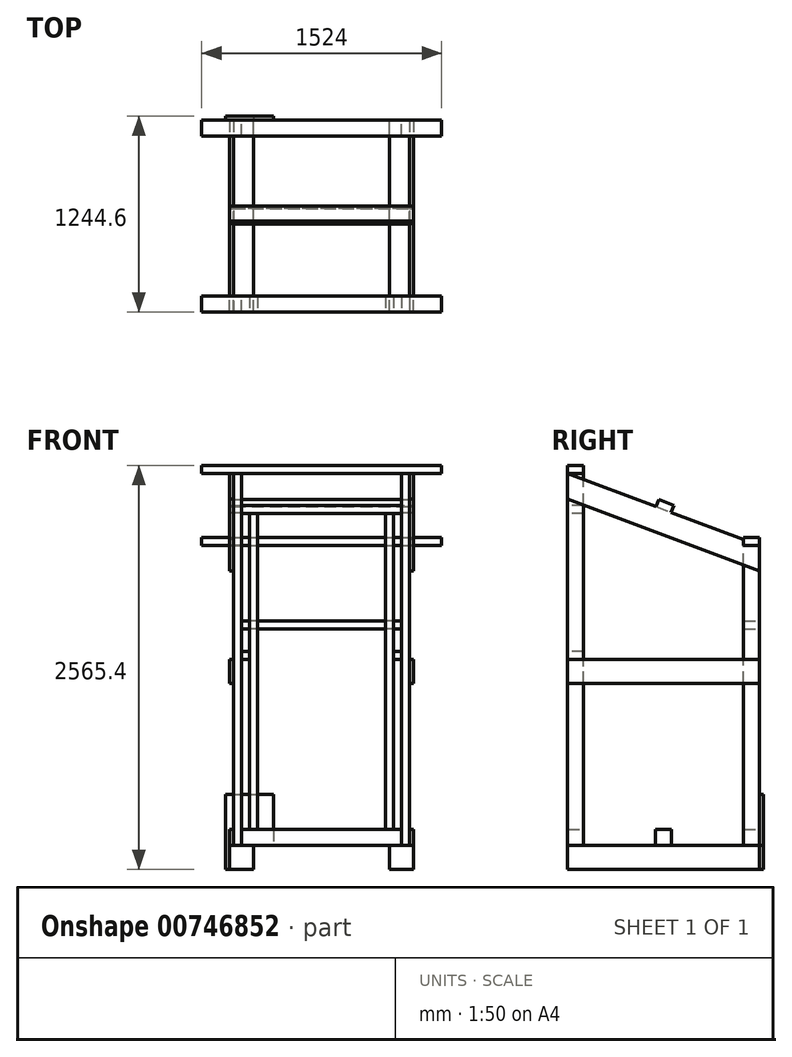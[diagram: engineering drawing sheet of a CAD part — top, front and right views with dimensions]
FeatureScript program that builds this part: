
annotation { "Feature Type Name" : "Feature", "Feature Type Description" : "" }
export const myFeature = defineFeature(function(context is Context, id is Id, definition is map)
    precondition{}
    {
        {
            var Q0;
            Q0=qCreatedBy(makeId("Front.planeOp"),FACE);
            var sketch = newSketch(context, id + "F0", { "sketchPlane" : qUnion([Q0])});
            skLineSegment(sketch, "E0.bottom", {"start": v(0, 0) * mm, "end": v(152.4, 0) * mm});
            skLineSegment(sketch, "E0.top", {"start": v(0, 152.4) * mm, "end": v(152.4, 152.4) * mm});
            skLineSegment(sketch, "E0.left", {"start": v(0, 0) * mm, "end": v(0, 152.4) * mm});
            skLineSegment(sketch, "E0.right", {"start": v(152.4, 0) * mm, "end": v(152.4, 152.4) * mm});
            skLineSegment(sketch, "E1.bottom", {"start": v(1016, 0) * mm, "end": v(1168.4, 0) * mm});
            skLineSegment(sketch, "E1.top", {"start": v(1016, 152.4) * mm, "end": v(1168.4, 152.4) * mm});
            skLineSegment(sketch, "E1.left", {"start": v(1016, 0) * mm, "end": v(1016, 152.4) * mm});
            skLineSegment(sketch, "E1.right", {"start": v(1168.4, 0) * mm, "end": v(1168.4, 152.4) * mm});
            skLineSegment(sketch, "E2.bottom", {"start": v(0, 152.4) * mm, "end": v(1168.4, 152.4) * mm});
            skLineSegment(sketch, "E2.top", {"start": v(0, 254) * mm, "end": v(1168.4, 254) * mm});
            skLineSegment(sketch, "E2.left", {"start": v(0, 152.4) * mm, "end": v(0, 254) * mm});
            skLineSegment(sketch, "E2.right", {"start": v(1168.4, 152.4) * mm, "end": v(1168.4, 254) * mm});
            skLineSegment(sketch, "E3.bottom", {"start": v(0, 152.4) * mm, "end": v(76.2, 152.4) * mm});
            skLineSegment(sketch, "E3.top", {"start": v(0, 254) * mm, "end": v(76.2, 254) * mm});
            skLineSegment(sketch, "E3.right", {"start": v(76.2, 152.4) * mm, "end": v(76.2, 254) * mm});
            skLineSegment(sketch, "E4.bottom", {"start": v(1168.4, 254) * mm, "end": v(1092.2, 254) * mm});
            skLineSegment(sketch, "E4.top", {"start": v(1168.4, 152.4) * mm, "end": v(1092.2, 152.4) * mm});
            skLineSegment(sketch, "E4.left", {"start": v(1168.4, 254) * mm, "end": v(1168.4, 152.4) * mm});
            skLineSegment(sketch, "E4.right", {"start": v(1092.2, 254) * mm, "end": v(1092.2, 152.4) * mm});
            skSolve(sketch);
        }
        {
            var Q0;
            Q0=makeQuery(id+"F0.imprint","IMPRINT",FACE,{"disambiguationData":[TD([[makeQuery(id+"F0.imprint","IMPRINT",EDGE,{"derivedFrom":sQuery(id+"F0.wireOp",EDGE,"E0.bottom")}),1.0]])]});
            var Q1;
            Q1=makeQuery(id+"F0.imprint","IMPRINT",FACE,{"disambiguationData":[TD([[makeQuery(id+"F0.imprint","IMPRINT",EDGE,{"derivedFrom":sQuery(id+"F0.wireOp",EDGE,"E1.bottom")}),1.0]])]});
            extrude(context, id + "F1", {"entities" : qUnion([Q0, Q1]), "depth" : 1219.2 * mm, "offsetDistance" : 25 * mm});
        }
        {
            var Q0;
            {var subQ3=sQuery(id+"F0.wireOp",EDGE,"E2.bottom");Q0=makeQuery(id+"F0.imprint","IMPRINT",FACE,{"disambiguationData":[TD([[makeQuery(id+"F0.imprint","IMPRINT",EDGE,{"derivedFrom":subQ3}),1.0]])]});}
            extrude(context, id + "F2", {"entities" : qUnion([Q0]), "depth" : 101.6 * mm, "offsetDistance" : 25 * mm});
        }
        {
            var Q0;
            Q0=makeQuery(id+"F2.opExtrude","SWEPT_BODY",BODY,{"disambiguationData":[OSD([sQuery(id+"F0.wireOp",EDGE,"E0.top"),sQuery(id+"F0.wireOp",EDGE,"E1.top"),sQuery(id+"F0.wireOp",EDGE,"E2.bottom"),sQuery(id+"F0.wireOp",EDGE,"E2.top"),sQuery(id+"F0.wireOp",EDGE,"E3.right"),sQuery(id+"F0.wireOp",EDGE,"E4.right")])]});
            var Q1;
            Q1=makeQuery(id+"F2.opExtrude","CAP_FACE",FACE,{"disambiguationData":[OSD([sQuery(id+"F0.wireOp",EDGE,"E0.top"),sQuery(id+"F0.wireOp",EDGE,"E1.top"),sQuery(id+"F0.wireOp",EDGE,"E2.bottom"),sQuery(id+"F0.wireOp",EDGE,"E2.top"),sQuery(id+"F0.wireOp",EDGE,"E3.right"),sQuery(id+"F0.wireOp",EDGE,"E4.right")])],"isStart":false});
            transform(context, id + "F3", {"entities" : qUnion([Q0]), "transformType" : TransformType.TRANSLATION_DISTANCE, "transformDirection" : qUnion([Q1]), "distance" : 1117.6 * mm, "makeCopy" : true});
        }
        {
            var Q0;
            Q0=makeQuery(id+"F1.opExtrude","SWEPT_FACE",FACE,{"disambiguationData":[OSD([sQuery(id+"F0.wireOp",EDGE,"E0.top")])]});
            var sketch = newSketch(context, id + "F4", { "sketchPlane" : qUnion([Q0])});
            skLineSegment(sketch, "E5.bottom", {"start": v(0, -609.6) * mm, "end": v(1168.4, -609.6) * mm});
            skLineSegment(sketch, "E5.top", {"start": v(0, -660.4) * mm, "end": v(1168.4, -660.4) * mm});
            skLineSegment(sketch, "E5.left", {"start": v(0, -609.6) * mm, "end": v(0, -660.4) * mm});
            skLineSegment(sketch, "E5.right", {"start": v(1168.4, -609.6) * mm, "end": v(1168.4, -660.4) * mm});
            skLineSegment(sketch, "E6.MirrorCS", {"start": v(0, -609.6) * mm, "end": v(0, -558.8) * mm});
            skLineSegment(sketch, "E7.MirrorCS", {"start": v(0, -558.8) * mm, "end": v(1168.4, -558.8) * mm});
            skLineSegment(sketch, "E8.MirrorCS", {"start": v(1168.4, -609.6) * mm, "end": v(1168.4, -558.8) * mm});
            skSolve(sketch);
        }
        {
            var Q0;
            {var subQ0=sQuery(id+"F4.wireOp",EDGE,"E6.MirrorCS");Q0=makeQuery(id+"F4.imprint","IMPRINT",FACE,{"disambiguationData":[TD([[makeQuery(id+"F4.imprint","IMPRINT",EDGE,{"derivedFrom":subQ0}),-1.0]])]});}
            var Q1;
            {var subQ0=sQuery(id+"F4.wireOp",EDGE,"E5.left");Q1=makeQuery(id+"F4.imprint","IMPRINT",FACE,{"disambiguationData":[TD([[makeQuery(id+"F4.imprint","IMPRINT",EDGE,{"derivedFrom":subQ0}),-1.0]])]});}
            var Q2;
            {var subQ0=sQuery(id+"F4.wireOp",EDGE,"E5.right");Q2=makeQuery(id+"F4.imprint","IMPRINT",FACE,{"disambiguationData":[TD([[makeQuery(id+"F4.imprint","IMPRINT",EDGE,{"derivedFrom":subQ0}),-1.0]])]});}
            var Q3;
            {var subQ0=sQuery(id+"F4.wireOp",EDGE,"E8.MirrorCS");Q3=makeQuery(id+"F4.imprint","IMPRINT",FACE,{"disambiguationData":[TD([[makeQuery(id+"F4.imprint","IMPRINT",EDGE,{"derivedFrom":subQ0}),1.0]])]});}
            extrude(context, id + "F5", {"entities" : qUnion([Q0, Q1, Q2, Q3]), "depth" : 101.6 * mm, "offsetDistance" : 25 * mm});
        }
        {
            var Q0;
            Q0=makeQuery(id+"F3.opPattern","COPY",FACE,{"derivedFrom":makeQuery(id+"F2.opExtrude","CAP_FACE",FACE,{"disambiguationData":[OSD([sQuery(id+"F0.wireOp",EDGE,"E0.top"),sQuery(id+"F0.wireOp",EDGE,"E1.top"),sQuery(id+"F0.wireOp",EDGE,"E2.bottom"),sQuery(id+"F0.wireOp",EDGE,"E2.top"),sQuery(id+"F0.wireOp",EDGE,"E3.right"),sQuery(id+"F0.wireOp",EDGE,"E4.right")])],"isStart":false}),"instanceName":"1"});
            var sketch = newSketch(context, id + "F6", { "sketchPlane" : qUnion([Q0])});
            skLineSegment(sketch, "E9.bottom", {"start": v(76.2, 152.4) * mm, "end": v(25.4, 152.4) * mm});
            skLineSegment(sketch, "E9.top", {"start": v(76.2, 2514.6) * mm, "end": v(25.4, 2514.6) * mm});
            skLineSegment(sketch, "E9.left", {"start": v(76.2, 152.4) * mm, "end": v(76.2, 2514.6) * mm});
            skLineSegment(sketch, "E9.right", {"start": v(25.4, 152.4) * mm, "end": v(25.4, 2514.6) * mm});
            skLineSegment(sketch, "E10.bottom", {"start": v(1092.2, 152.4) * mm, "end": v(1143, 152.4) * mm});
            skLineSegment(sketch, "E10.top", {"start": v(1092.2, 2514.6) * mm, "end": v(1143, 2514.6) * mm});
            skLineSegment(sketch, "E10.left", {"start": v(1092.2, 152.4) * mm, "end": v(1092.2, 2514.6) * mm});
            skLineSegment(sketch, "E10.right", {"start": v(1143, 152.4) * mm, "end": v(1143, 2514.6) * mm});
            skLineSegment(sketch, "E11.bottom", {"start": v(127, 254) * mm, "end": v(177.8, 254) * mm});
            skLineSegment(sketch, "E11.top", {"start": v(127, 2260.6) * mm, "end": v(177.8, 2260.6) * mm});
            skLineSegment(sketch, "E11.left", {"start": v(127, 254) * mm, "end": v(127, 2260.6) * mm});
            skLineSegment(sketch, "E11.right", {"start": v(177.8, 254) * mm, "end": v(177.8, 2260.6) * mm});
            skLineSegment(sketch, "E12.bottom", {"start": v(1041.4, 254) * mm, "end": v(990.6, 254) * mm});
            skLineSegment(sketch, "E12.top", {"start": v(1041.4, 2260.6) * mm, "end": v(990.6, 2260.6) * mm});
            skLineSegment(sketch, "E12.left", {"start": v(1041.4, 254) * mm, "end": v(1041.4, 2260.6) * mm});
            skLineSegment(sketch, "E12.right", {"start": v(990.6, 254) * mm, "end": v(990.6, 2260.6) * mm});
            skLineSegment(sketch, "E13.bottom", {"start": v(76.2, 2260.6) * mm, "end": v(1092.2, 2260.6) * mm});
            skLineSegment(sketch, "E13.top", {"start": v(76.2, 2311.4) * mm, "end": v(1092.2, 2311.4) * mm});
            skLineSegment(sketch, "E13.left", {"start": v(76.2, 2260.6) * mm, "end": v(76.2, 2311.4) * mm});
            skLineSegment(sketch, "E13.right", {"start": v(1092.2, 2260.6) * mm, "end": v(1092.2, 2311.4) * mm});
            skLineSegment(sketch, "E14", {"start": v(584.2, 2311.4) * mm, "end": v(584.2, 2514.6) * mm, "construction": true});
            skLineSegment(sketch, "E15.bottom", {"start": v(584.2, 2514.6) * mm, "end": v(-177.8, 2514.6) * mm});
            skLineSegment(sketch, "E15.top", {"start": v(584.2, 2565.4) * mm, "end": v(-177.8, 2565.4) * mm});
            skLineSegment(sketch, "E15.left", {"start": v(584.2, 2514.6) * mm, "end": v(584.2, 2565.4) * mm});
            skLineSegment(sketch, "E15.right", {"start": v(-177.8, 2514.6) * mm, "end": v(-177.8, 2565.4) * mm});
            skLineSegment(sketch, "E16.MirrorCS", {"start": v(584.2, 2565.4) * mm, "end": v(1346.2, 2565.4) * mm});
            skLineSegment(sketch, "E17.MirrorCS", {"start": v(584.2, 2514.6) * mm, "end": v(1346.2, 2514.6) * mm});
            skLineSegment(sketch, "E18.MirrorCS", {"start": v(1346.2, 2514.6) * mm, "end": v(1346.2, 2565.4) * mm});
            skLineSegment(sketch, "E19.bottom", {"start": v(25.4, 1333.5) * mm, "end": v(0, 1333.5) * mm});
            skLineSegment(sketch, "E19.top", {"start": v(25.4, 1181.1) * mm, "end": v(0, 1181.1) * mm});
            skLineSegment(sketch, "E19.left", {"start": v(25.4, 1333.5) * mm, "end": v(25.4, 1181.1) * mm});
            skLineSegment(sketch, "E19.right", {"start": v(0, 1333.5) * mm, "end": v(0, 1181.1) * mm});
            skLineSegment(sketch, "E20.bottom", {"start": v(1143, 1333.5) * mm, "end": v(1168.4, 1333.5) * mm});
            skLineSegment(sketch, "E20.top", {"start": v(1143, 1181.1) * mm, "end": v(1168.4, 1181.1) * mm});
            skLineSegment(sketch, "E20.left", {"start": v(1143, 1333.5) * mm, "end": v(1143, 1181.1) * mm});
            skLineSegment(sketch, "E20.right", {"start": v(1168.4, 1333.5) * mm, "end": v(1168.4, 1181.1) * mm});
            skLineSegment(sketch, "E21.bottom", {"start": v(76.2, 1333.5) * mm, "end": v(127, 1333.5) * mm});
            skLineSegment(sketch, "E21.top", {"start": v(76.2, 1384.3) * mm, "end": v(127, 1384.3) * mm});
            skLineSegment(sketch, "E21.left", {"start": v(76.2, 1333.5) * mm, "end": v(76.2, 1384.3) * mm});
            skLineSegment(sketch, "E21.right", {"start": v(127, 1333.5) * mm, "end": v(127, 1384.3) * mm});
            skLineSegment(sketch, "E22.bottom", {"start": v(1092.2, 1333.5) * mm, "end": v(1041.4, 1333.5) * mm});
            skLineSegment(sketch, "E22.top", {"start": v(1092.2, 1384.3) * mm, "end": v(1041.4, 1384.3) * mm});
            skLineSegment(sketch, "E22.left", {"start": v(1092.2, 1333.5) * mm, "end": v(1092.2, 1384.3) * mm});
            skLineSegment(sketch, "E22.right", {"start": v(1041.4, 1333.5) * mm, "end": v(1041.4, 1384.3) * mm});
            skSolve(sketch);
        }
        {
            var Q0;
            {var subQ1=sQuery(id+"F6.wireOp",EDGE,"E9.bottom");Q0=makeQuery(id+"F6.imprint","IMPRINT",FACE,{"disambiguationData":[TD([[makeQuery(id+"F6.imprint","IMPRINT",EDGE,{"derivedFrom":subQ1}),-1.0]])]});}
            var Q1;
            {var subQ3=sQuery(id+"F6.wireOp",EDGE,"E10.bottom");Q1=makeQuery(id+"F6.imprint","IMPRINT",FACE,{"disambiguationData":[TD([[makeQuery(id+"F6.imprint","IMPRINT",EDGE,{"derivedFrom":subQ3}),1.0]])]});}
            extrude(context, id + "F7", {"entities" : qUnion([Q0, Q1]), "depth" : -101.6 * mm, "offsetDistance" : 25 * mm});
        }
        {
            var Q0;
            Q0=makeQuery(id+"F2.opExtrude","CAP_FACE",FACE,{"disambiguationData":[OSD([sQuery(id+"F0.wireOp",EDGE,"E0.top"),sQuery(id+"F0.wireOp",EDGE,"E1.top"),sQuery(id+"F0.wireOp",EDGE,"E2.bottom"),sQuery(id+"F0.wireOp",EDGE,"E2.top"),sQuery(id+"F0.wireOp",EDGE,"E3.right"),sQuery(id+"F0.wireOp",EDGE,"E4.right")])],"isStart":true});
            var sketch = newSketch(context, id + "F8", { "sketchPlane" : qUnion([Q0])});
            skLineSegment(sketch, "E23.bottom", {"start": v(-1092.2, 152.4) * mm, "end": v(-1143, 152.4) * mm});
            skLineSegment(sketch, "E23.top", {"start": v(-1092.2, 2057.4) * mm, "end": v(-1143, 2057.4) * mm});
            skLineSegment(sketch, "E23.left", {"start": v(-1092.2, 152.4) * mm, "end": v(-1092.2, 2057.4) * mm});
            skLineSegment(sketch, "E23.right", {"start": v(-1143, 152.4) * mm, "end": v(-1143, 2057.4) * mm});
            skLineSegment(sketch, "E24.bottom", {"start": v(-76.2, 152.4) * mm, "end": v(-25.4, 152.4) * mm});
            skLineSegment(sketch, "E24.top", {"start": v(-76.2, 2057.4) * mm, "end": v(-25.4, 2057.4) * mm});
            skLineSegment(sketch, "E24.left", {"start": v(-76.2, 152.4) * mm, "end": v(-76.2, 2057.4) * mm});
            skLineSegment(sketch, "E24.right", {"start": v(-25.4, 152.4) * mm, "end": v(-25.4, 2057.4) * mm});
            skSolve(sketch);
        }
        {
            var Q0;
            {var subQ1=sQuery(id+"F8.wireOp",EDGE,"E23.bottom");Q0=makeQuery(id+"F8.imprint","IMPRINT",FACE,{"disambiguationData":[TD([[makeQuery(id+"F8.imprint","IMPRINT",EDGE,{"derivedFrom":subQ1}),-1.0]])]});}
            var Q1;
            {var subQ1=sQuery(id+"F8.wireOp",EDGE,"E24.bottom");Q1=makeQuery(id+"F8.imprint","IMPRINT",FACE,{"disambiguationData":[TD([[makeQuery(id+"F8.imprint","IMPRINT",EDGE,{"derivedFrom":subQ1}),1.0]])]});}
            extrude(context, id + "F9", {"entities" : qUnion([Q0, Q1]), "depth" : -101.6 * mm, "offsetDistance" : 25 * mm});
        }
        {
            var Q0;
            Q0=makeQuery(id+"F6.imprint","IMPRINT",FACE,{"disambiguationData":[TD([[makeQuery(id+"F6.imprint","IMPRINT",EDGE,{"derivedFrom":sQuery(id+"F6.wireOp",EDGE,"E11.bottom")}),1.0]])]});
            var Q1;
            Q1=makeQuery(id+"F6.imprint","IMPRINT",FACE,{"disambiguationData":[TD([[makeQuery(id+"F6.imprint","IMPRINT",EDGE,{"derivedFrom":sQuery(id+"F6.wireOp",EDGE,"E12.bottom")}),1.0]])]});
            extrude(context, id + "F10", {"entities" : qUnion([Q0, Q1]), "depth" : -101.6 * mm, "offsetDistance" : 25 * mm});
        }
        {
            var Q0;
            Q0=makeQuery(id+"F6.imprint","IMPRINT",FACE,{"disambiguationData":[TD([[makeQuery(id+"F6.imprint","IMPRINT",EDGE,{"derivedFrom":sQuery(id+"F6.wireOp",EDGE,"E13.top")}),-1.0]])]});
            var Q1;
            {var subQ3=sQuery(id+"F6.wireOp",EDGE,"E15.left");Q1=makeQuery(id+"F6.imprint","IMPRINT",FACE,{"disambiguationData":[TD([[makeQuery(id+"F6.imprint","IMPRINT",EDGE,{"derivedFrom":subQ3}),-1.0]])]});}
            var Q2;
            Q2=makeQuery(id+"F6.imprint","IMPRINT",FACE,{"disambiguationData":[TD([[makeQuery(id+"F6.imprint","IMPRINT",EDGE,{"derivedFrom":sQuery(id+"F6.wireOp",EDGE,"E15.top")}),1.0]])]});
            extrude(context, id + "F11", {"entities" : qUnion([Q0, Q1, Q2]), "depth" : -101.6 * mm, "offsetDistance" : 25 * mm});
        }
        {
            var Q0;
            Q0=makeQuery(id+"F7.opExtrude","SWEPT_FACE",FACE,{"disambiguationData":[OSD([sQuery(id+"F6.wireOp",EDGE,"E10.right")])]});
            var sketch = newSketch(context, id + "F12", { "sketchPlane" : qUnion([Q0])});
            skLineSegment(sketch, "E25", {"start": v(-1219.2, 2514.6) * mm, "end": v(0, 2057.41) * mm});
            skLineSegment(sketch, "E26", {"start": v(0, 2057.41) * mm, "end": v(0, 1894.65) * mm});
            skLineSegment(sketch, "E27", {"start": v(0, 1894.65) * mm, "end": v(-1219.2, 2351.84) * mm});
            skLineSegment(sketch, "E28", {"start": v(-1219.2, 2351.84) * mm, "end": v(-1219.2, 2514.6) * mm});
            skLineSegment(sketch, "E29", {"start": v(-1219.2, 2351.84) * mm, "end": v(-1219.2, 152.4) * mm, "construction": true});
            skLineSegment(sketch, "E30", {"start": v(-1219.2, 152.4) * mm, "end": v(0, 152.4) * mm, "construction": true});
            skPoint(sketch, "E30.endSnap0", {"position": v(-1168.4, 152.4) * mm});
            skLineSegment(sketch, "E31", {"start": v(0, 152.4) * mm, "end": v(0, 1894.65) * mm, "construction": true});
            skLineSegment(sketch, "E32", {"start": v(0, 2057.41) * mm, "end": v(-101.6, 2057.41) * mm});
            skLineSegment(sketch, "E33", {"start": v(-101.6, 2057.41) * mm, "end": v(-101.6, 2095.51) * mm});
            skLineSegment(sketch, "E34", {"start": v(-609.6, 2286) * mm, "end": v(-592.83, 2330.73) * mm});
            skLineSegment(sketch, "E35", {"start": v(-592.83, 2330.73) * mm, "end": v(-545.26, 2312.9) * mm});
            skLineSegment(sketch, "E36", {"start": v(-545.26, 2312.9) * mm, "end": v(-562.03, 2268.17) * mm});
            skLineSegment(sketch, "E37.MirrorCS", {"start": v(-592.83, 2330.73) * mm, "end": v(-640.4, 2348.57) * mm});
            skLineSegment(sketch, "E38.MirrorCS", {"start": v(0, 2057.41) * mm, "end": v(-1219.2, 2514.6) * mm});
            skLineSegment(sketch, "E39.MirrorCS", {"start": v(-640.4, 2348.57) * mm, "end": v(-657.17, 2303.84) * mm});
            skSolve(sketch);
        }
        {
            var Q0;
            {var subQ0=sQuery(id+"F12.wireOp",EDGE,"E26");Q0=makeQuery(id+"F12.imprint","IMPRINT",FACE,{"disambiguationData":[TD([[makeQuery(id+"F12.imprint","IMPRINT",EDGE,{"derivedFrom":subQ0}),-1.0]])]});}
            var Q1;
            {var subQ0=sQuery(id+"F12.wireOp",EDGE,"E28");Q1=makeQuery(id+"F12.imprint","IMPRINT",FACE,{"disambiguationData":[TD([[makeQuery(id+"F12.imprint","IMPRINT",EDGE,{"derivedFrom":subQ0}),-1.0]])]});}
            extrude(context, id + "F13", {"entities" : qUnion([Q0, Q1]), "depth" : 25.4 * mm, "offsetDistance" : 25 * mm});
        }
        {
            var Q0;
            {var subQ0=sQuery(id+"F12.wireOp",EDGE,"E34");Q0=makeQuery(id+"F12.imprint","IMPRINT",FACE,{"disambiguationData":[TD([[makeQuery(id+"F12.imprint","IMPRINT",EDGE,{"derivedFrom":subQ0}),1.0]])]});}
            var Q1;
            {var subQ0=sQuery(id+"F12.wireOp",EDGE,"E34");Q1=makeQuery(id+"F12.imprint","IMPRINT",FACE,{"disambiguationData":[TD([[makeQuery(id+"F12.imprint","IMPRINT",EDGE,{"derivedFrom":subQ0}),-1.0]])]});}
            extrude(context, id + "F14", {"entities" : qUnion([Q0, Q1]), "depth" : -1117.6 * mm, "offsetDistance" : 25 * mm});
        }
        {
            var Q0;
            Q0=makeQuery(id+"F13.opExtrude","SWEPT_BODY",BODY,{"disambiguationData":[OSD([sQuery(id+"F12.wireOp",EDGE,"E26"),sQuery(id+"F12.wireOp",EDGE,"E27"),sQuery(id+"F12.wireOp",EDGE,"E28"),sQuery(id+"F12.wireOp",EDGE,"E32"),sQuery(id+"F12.wireOp",EDGE,"E33"),sQuery(id+"F12.wireOp",EDGE,"E38.MirrorCS")])]});
            var Q1;
            Q1=makeQuery(id+"F13.opExtrude","CAP_FACE",FACE,{"disambiguationData":[OSD([sQuery(id+"F12.wireOp",EDGE,"E26"),sQuery(id+"F12.wireOp",EDGE,"E27"),sQuery(id+"F12.wireOp",EDGE,"E28"),sQuery(id+"F12.wireOp",EDGE,"E32"),sQuery(id+"F12.wireOp",EDGE,"E33"),sQuery(id+"F12.wireOp",EDGE,"E38.MirrorCS")])],"isStart":true});
            transform(context, id + "F15", {"entities" : qUnion([Q0]), "transformType" : TransformType.TRANSLATION_DISTANCE, "transformDirection" : qUnion([Q1]), "distance" : 1143 * mm, "makeCopy" : true});
        }
        {
            var Q0;
            Q0=makeQuery(id+"F14.opExtrude","CAP_FACE",FACE,{"disambiguationData":[OSD([sQuery(id+"F12.wireOp",EDGE,"E35"),sQuery(id+"F12.wireOp",EDGE,"E36"),sQuery(id+"F12.wireOp",EDGE,"E37.MirrorCS"),sQuery(id+"F12.wireOp",EDGE,"E38.MirrorCS"),sQuery(id+"F12.wireOp",EDGE,"E39.MirrorCS")])],"isStart":true});
            extrude(context, id + "F16", {"entities" : qUnion([Q0]), "operationType" : NewBodyOperationType.ADD, "depth" : 25.4 * mm, "offsetDistance" : 25 * mm});
        }
        {
            var Q0;
            Q0=makeQuery(id+"F14.opExtrude","CAP_FACE",FACE,{"disambiguationData":[OSD([sQuery(id+"F12.wireOp",EDGE,"E35"),sQuery(id+"F12.wireOp",EDGE,"E36"),sQuery(id+"F12.wireOp",EDGE,"E37.MirrorCS"),sQuery(id+"F12.wireOp",EDGE,"E38.MirrorCS"),sQuery(id+"F12.wireOp",EDGE,"E39.MirrorCS")])],"isStart":false});
            extrude(context, id + "F17", {"entities" : qUnion([Q0]), "operationType" : NewBodyOperationType.ADD, "depth" : 25.4 * mm, "offsetDistance" : 25 * mm});
        }
        {
            var Q0;
            Q0=makeQuery(id+"F6.imprint","IMPRINT",FACE,{"disambiguationData":[TD([[makeQuery(id+"F6.imprint","IMPRINT",EDGE,{"derivedFrom":sQuery(id+"F6.wireOp",EDGE,"E21.bottom")}),1.0]])]});
            var Q1;
            Q1=makeQuery(id+"F6.imprint","IMPRINT",FACE,{"disambiguationData":[TD([[makeQuery(id+"F6.imprint","IMPRINT",EDGE,{"derivedFrom":sQuery(id+"F6.wireOp",EDGE,"E22.bottom")}),-1.0]])]});
            extrude(context, id + "F18", {"entities" : qUnion([Q0, Q1]), "depth" : -101.6 * mm, "offsetDistance" : 25 * mm});
        }
        {
            var Q0;
            Q0=makeQuery(id+"F6.imprint","IMPRINT",FACE,{"disambiguationData":[TD([[makeQuery(id+"F6.imprint","IMPRINT",EDGE,{"derivedFrom":sQuery(id+"F6.wireOp",EDGE,"E19.bottom")}),1.0]])]});
            var Q1;
            Q1=makeQuery(id+"F6.imprint","IMPRINT",FACE,{"disambiguationData":[TD([[makeQuery(id+"F6.imprint","IMPRINT",EDGE,{"derivedFrom":sQuery(id+"F6.wireOp",EDGE,"E20.bottom")}),-1.0]])]});
            extrude(context, id + "F19", {"entities" : qUnion([Q0, Q1]), "depth" : -1219.2 * mm, "offsetDistance" : 25 * mm});
        }
        {
            var Q0;
            Q0=makeQuery(id+"F9.opExtrude","CAP_FACE",FACE,{"disambiguationData":[OSD([sQuery(id+"F8.wireOp",EDGE,"E23.bottom"),sQuery(id+"F8.wireOp",EDGE,"E23.top"),sQuery(id+"F8.wireOp",EDGE,"E23.left"),sQuery(id+"F8.wireOp",EDGE,"E23.right")])],"isStart":true});
            var sketch = newSketch(context, id + "F20", { "sketchPlane" : qUnion([Q0])});
            skLineSegment(sketch, "E40.bottom", {"start": v(-1092.2, 1528.52) * mm, "end": v(-76.2, 1528.52) * mm});
            skLineSegment(sketch, "E40.top", {"start": v(-1092.2, 1579.32) * mm, "end": v(-76.2, 1579.32) * mm});
            skLineSegment(sketch, "E40.left", {"start": v(-1092.2, 1528.52) * mm, "end": v(-1092.2, 1579.32) * mm});
            skLineSegment(sketch, "E40.right", {"start": v(-76.2, 1528.52) * mm, "end": v(-76.2, 1579.32) * mm});
            skLineSegment(sketch, "E41", {"start": v(-584.2, 1579.32) * mm, "end": v(-584.2, 2057.4) * mm, "construction": true});
            skLineSegment(sketch, "E42.bottom", {"start": v(-584.2, 2057.4) * mm, "end": v(-1346.2, 2057.4) * mm});
            skLineSegment(sketch, "E42.top", {"start": v(-584.2, 2108.2) * mm, "end": v(-1346.2, 2108.2) * mm});
            skLineSegment(sketch, "E42.left", {"start": v(-584.2, 2057.4) * mm, "end": v(-584.2, 2108.2) * mm});
            skLineSegment(sketch, "E42.right", {"start": v(-1346.2, 2057.4) * mm, "end": v(-1346.2, 2108.2) * mm});
            skLineSegment(sketch, "E43.MirrorCS", {"start": v(-584.2, 2108.2) * mm, "end": v(177.8, 2108.2) * mm});
            skLineSegment(sketch, "E44.MirrorCS", {"start": v(-584.2, 2057.4) * mm, "end": v(177.8, 2057.4) * mm});
            skLineSegment(sketch, "E45.MirrorCS", {"start": v(177.8, 2057.4) * mm, "end": v(177.8, 2108.2) * mm});
            skSolve(sketch);
        }
        {
            var Q0;
            Q0=makeQuery(id+"F20.imprint","IMPRINT",FACE,{"disambiguationData":[TD([[makeQuery(id+"F20.imprint","IMPRINT",EDGE,{"derivedFrom":sQuery(id+"F20.wireOp",EDGE,"E40.bottom")}),1.0]])]});
            var Q1;
            Q1=makeQuery(id+"F20.imprint","IMPRINT",FACE,{"disambiguationData":[TD([[makeQuery(id+"F20.imprint","IMPRINT",EDGE,{"derivedFrom":sQuery(id+"F20.wireOp",EDGE,"E42.top")}),1.0]])]});
            var Q2;
            Q2=makeQuery(id+"F20.imprint","IMPRINT",FACE,{"disambiguationData":[TD([[makeQuery(id+"F20.imprint","IMPRINT",EDGE,{"derivedFrom":sQuery(id+"F20.wireOp",EDGE,"E42.left")}),-1.0]])]});
            extrude(context, id + "F21", {"entities" : qUnion([Q0, Q1, Q2]), "depth" : -101.6 * mm, "offsetDistance" : 25 * mm});
        }
        {
            var Q0;
            Q0=makeQuery(id+"F1.opExtrude","CAP_FACE",FACE,{"disambiguationData":[OSD([sQuery(id+"F0.wireOp",EDGE,"E0.bottom"),sQuery(id+"F0.wireOp",EDGE,"E0.top"),sQuery(id+"F0.wireOp",EDGE,"E0.left"),sQuery(id+"F0.wireOp",EDGE,"E0.right")])],"isStart":true});
            var sketch = newSketch(context, id + "F22", { "sketchPlane" : qUnion([Q0])});
            skLineSegment(sketch, "E46", {"start": v(25.4, 0) * mm, "end": v(25.4, 475.34) * mm});
            skLineSegment(sketch, "E47", {"start": v(25.4, 475.34) * mm, "end": v(-279.4, 475.34) * mm});
            skLineSegment(sketch, "E48", {"start": v(-279.4, 475.34) * mm, "end": v(-279.4, 152.4) * mm});
            skLineSegment(sketch, "E49", {"start": v(-279.4, 152.4) * mm, "end": v(-152.4, 152.4) * mm});
            skLineSegment(sketch, "E50", {"start": v(-152.4, 152.4) * mm, "end": v(-152.4, 0) * mm});
            skLineSegment(sketch, "E51", {"start": v(-152.4, 0) * mm, "end": v(25.4, 0) * mm});
            skSolve(sketch);
        }
        {
            var Q0;
            {var subQ0=sQuery(id+"F22.wireOp",EDGE,"E46");Q0=makeQuery(id+"F22.imprint","IMPRINT",FACE,{"disambiguationData":[TD([[makeQuery(id+"F22.imprint","IMPRINT",EDGE,{"derivedFrom":subQ0}),1.0]])]});}
            var Q1;
            {var subQ0=sQuery(id+"F22.wireOp",EDGE,"E50");Q1=makeQuery(id+"F22.imprint","IMPRINT",FACE,{"disambiguationData":[TD([[makeQuery(id+"F22.imprint","IMPRINT",EDGE,{"derivedFrom":subQ0}),-1.0]])]});}
            extrude(context, id + "F23", {"entities" : qUnion([Q0, Q1]), "depth" : 25.4 * mm, "offsetDistance" : 25 * mm});
        }
    });
